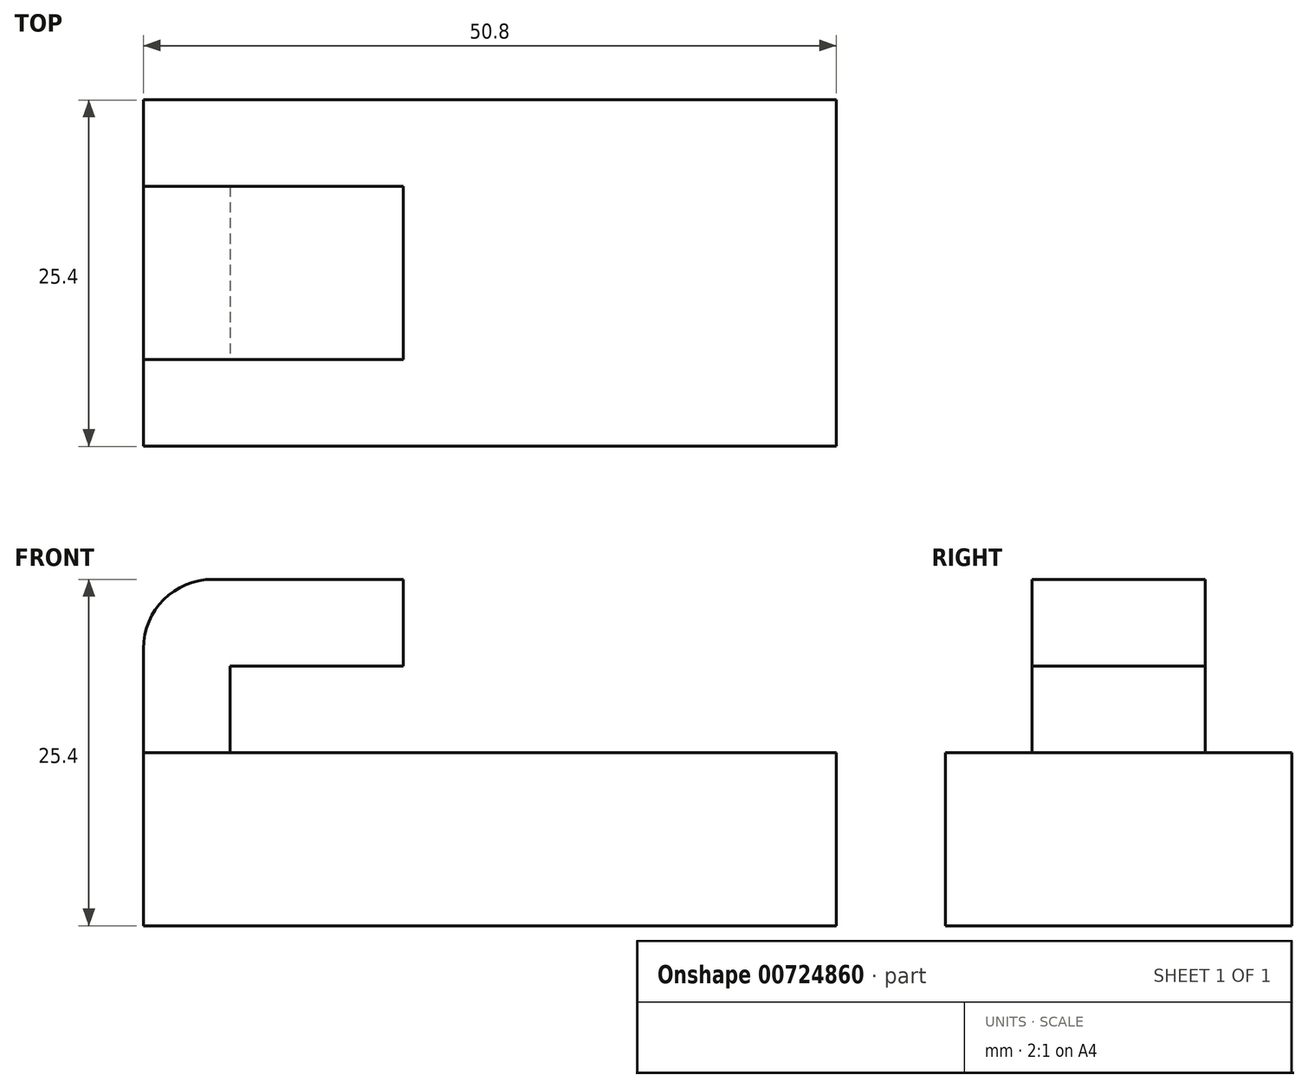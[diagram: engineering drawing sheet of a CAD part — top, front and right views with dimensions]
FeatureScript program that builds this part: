
annotation { "Feature Type Name" : "Feature", "Feature Type Description" : "" }
export const myFeature = defineFeature(function(context is Context, id is Id, definition is map)
    precondition{}
    {
        {
            var Q0;
            Q0=qCreatedBy(makeId("Top.planeOp"),FACE);
            var sketch = newSketch(context, id + "F0", { "sketchPlane" : qUnion([Q0])});
            skLineSegment(sketch, "E0.bottom", {"start": v(19.6, -13.96) * mm, "end": v(-31.2, -13.96) * mm});
            skLineSegment(sketch, "E0.top", {"start": v(19.6, 11.44) * mm, "end": v(-31.2, 11.44) * mm});
            skLineSegment(sketch, "E0.left", {"start": v(19.6, -13.96) * mm, "end": v(19.6, 11.44) * mm});
            skLineSegment(sketch, "E0.right", {"start": v(-31.2, -13.96) * mm, "end": v(-31.2, 11.44) * mm});
            skSolve(sketch);
        }
        {
            var Q0;
            Q0=makeQuery(id+"F0.imprint","IMPRINT",FACE,{"disambiguationData":[TD([[makeQuery(id+"F0.imprint","IMPRINT",EDGE,{"derivedFrom":sQuery(id+"F0.wireOp",EDGE,"E0.bottom")}),-1.0]])]});
            extrude(context, id + "F1", {"entities" : qUnion([Q0]), "depth" : 12.7 * mm, "offsetDistance" : 25.4 * mm});
        }
        {
            var Q0;
            Q0=makeQuery(id+"F1.opExtrude","CAP_FACE",FACE,{"disambiguationData":[OSD([sQuery(id+"F0.wireOp",EDGE,"E0.bottom"),sQuery(id+"F0.wireOp",EDGE,"E0.top"),sQuery(id+"F0.wireOp",EDGE,"E0.left"),sQuery(id+"F0.wireOp",EDGE,"E0.right")])],"isStart":false});
            var sketch = newSketch(context, id + "F2", { "sketchPlane" : qUnion([Q0])});
            skLineSegment(sketch, "E1.bottom", {"start": v(-31.2, -7.6) * mm, "end": v(-12.15, -7.6) * mm});
            skLineSegment(sketch, "E1.top", {"start": v(-31.2, 5.1) * mm, "end": v(-12.15, 5.1) * mm});
            skLineSegment(sketch, "E1.left", {"start": v(-31.2, -7.6) * mm, "end": v(-31.2, 5.1) * mm});
            skLineSegment(sketch, "E1.right", {"start": v(-12.15, -7.6) * mm, "end": v(-12.15, 5.1) * mm});
            skSolve(sketch);
        }
        {
            var Q0;
            Q0 = qSketchRegion(id + "F2", true);
            extrude(context, id + "F3", {"entities" : qUnion([Q0]), "operationType" : NewBodyOperationType.ADD, "depth" : 12.7 * mm, "offsetDistance" : 25.4 * mm});
        }
        {
            var Q0;
            Q0=makeQuery(id+"F3.opExtrude","SWEPT_FACE",FACE,{"disambiguationData":[OSD([sQuery(id+"F2.wireOp",EDGE,"E1.bottom")])]});
            var sketch = newSketch(context, id + "F4", { "sketchPlane" : qUnion([Q0])});
            skLineSegment(sketch, "E2.bottom", {"start": v(-12.15, 12.7) * mm, "end": v(-24.85, 12.7) * mm});
            skLineSegment(sketch, "E2.top", {"start": v(-12.15, 19.05) * mm, "end": v(-24.85, 19.05) * mm});
            skLineSegment(sketch, "E2.left", {"start": v(-12.15, 12.7) * mm, "end": v(-12.15, 19.05) * mm});
            skLineSegment(sketch, "E2.right", {"start": v(-24.85, 12.7) * mm, "end": v(-24.85, 19.05) * mm});
            skLineSegment(sketch, "E3", {"start": v(-24.85, 12.7) * mm, "end": v(-28.03, 12.7) * mm});
            skLineSegment(sketch, "E4", {"start": v(-28.03, 12.7) * mm, "end": v(-24.85, 12.7) * mm});
            skSolve(sketch);
        }
        {
            var Q0;
            Q0 = qSketchRegion(id + "F4", true);
            extrude(context, id + "F5", {"entities" : qUnion([Q0]), "operationType" : NewBodyOperationType.REMOVE, "endBound" : BoundingType.UP_TO_NEXT, "oppositeDirection" : true, "depth" : 25.4 * mm, "offsetDistance" : 25.4 * mm});
        }
        {
            var Q0;
            Q0=makeQuery(id+"F3.opExtrude","CAP_EDGE",EDGE,{"disambiguationData":[OSD([sQuery(id+"F2.wireOp",EDGE,"E1.left")])],"isStart":false});
            fillet(context, id + "F6", {"entities" : qUnion([Q0]), "radius" : 5.08 * mm, "tangentPropagation" : true, "allowEdgeOverflow" : false});
        }
    });
